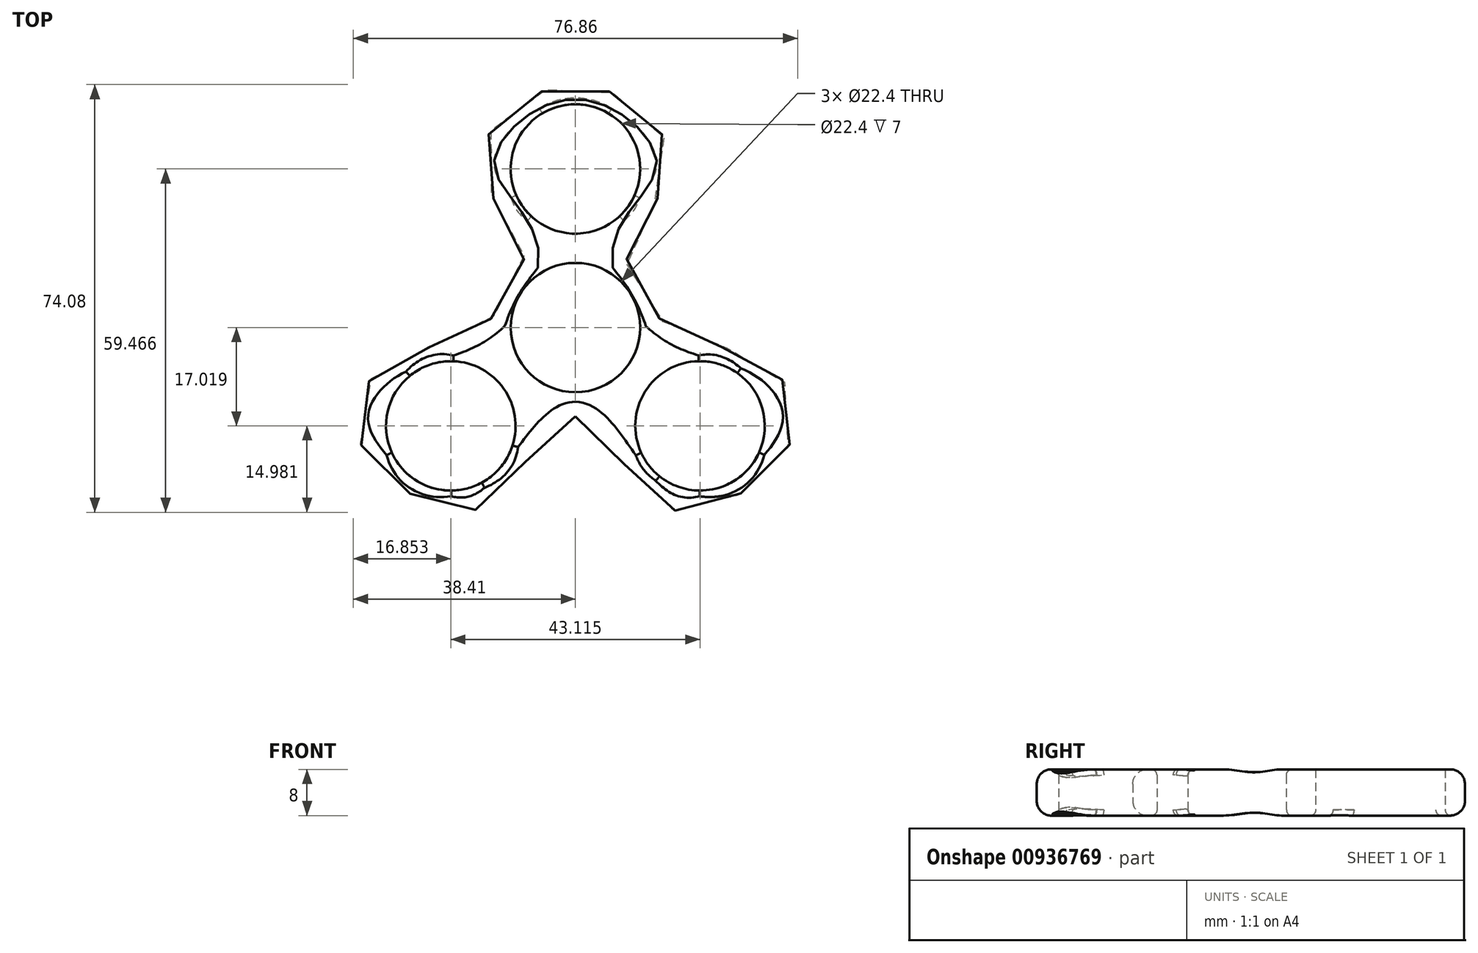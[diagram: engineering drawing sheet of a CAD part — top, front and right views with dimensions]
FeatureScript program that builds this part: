
annotation { "Feature Type Name" : "Feature", "Feature Type Description" : "" }
export const myFeature = defineFeature(function(context is Context, id is Id, definition is map)
    precondition{}
    {
        {
            var Q0;
            Q0=qCreatedBy(makeId("Top.planeOp"),FACE);
            var sketch = newSketch(context, id + "F0", { "sketchPlane" : qUnion([Q0])});
            skCircle(sketch, "E0", {"center": v(0, 0) * mm, "radius": 11.2 * mm});
            skPoint(sketch, "E1", {"position": v(-21.56, -17.02) * mm});
            skPoint(sketch, "E2.MirrorP", {"position": v(21.56, -17.02) * mm});
            skPoint(sketch, "E3", {"position": v(0, 27.47) * mm});
            skCircle(sketch, "E4", {"center": v(0, 27.47) * mm, "radius": 11.2 * mm});
            skCircle(sketch, "E5", {"center": v(21.56, -17.02) * mm, "radius": 11.2 * mm});
            skCircle(sketch, "E6", {"center": v(-21.56, -17.02) * mm, "radius": 11.2 * mm});
            skPoint(sketch, "E7", {"position": v(-16.63, 0) * mm});
            skPoint(sketch, "E8", {"position": v(-16.63, 28.38) * mm});
            skPoint(sketch, "E9", {"position": v(-38.24, -17.32) * mm});
            skPoint(sketch, "E10", {"position": v(-21.9, -31.73) * mm});
            skPoint(sketch, "E11", {"position": v(0, 42.08) * mm});
            skPoint(sketch, "E12", {"position": v(-9.07, 13.96) * mm});
            skPoint(sketch, "E13.MirrorP", {"position": v(16.63, 28.38) * mm});
            skPoint(sketch, "E14.MirrorP", {"position": v(9.07, 13.96) * mm});
            skPoint(sketch, "E15.MirrorP", {"position": v(16.63, 0) * mm});
            skPoint(sketch, "E16.MirrorP", {"position": v(38.24, -17.32) * mm});
            skPoint(sketch, "E17.MirrorP", {"position": v(21.9, -31.73) * mm});
            skPoint(sketch, "E18", {"position": v(0, -15.39) * mm});
            skPoint(sketch, "E19", {"position": v(-31.21, -5.72) * mm});
            skPoint(sketch, "E20", {"position": v(-11.35, -26.81) * mm});
            skPoint(sketch, "E21", {"position": v(31.7, -5.72) * mm});
            skPoint(sketch, "E22", {"position": v(10.8, -26.81) * mm});
            skFitSpline(sketch, "E23", {"points": [v(0, -15.39) * mm, v(-11.35, -26.81) * mm, v(-21.9, -31.73) * mm, v(-38.24, -17.32) * mm, v(-31.21, -5.72) * mm, v(-16.63, 0) * mm, v(-9.07, 13.96) * mm, v(-16.63, 28.38) * mm, v(0, 42.08) * mm, v(16.63, 28.38) * mm, v(9.07, 13.96) * mm, v(16.63, 0) * mm, v(31.7, -5.72) * mm, v(38.24, -17.32) * mm, v(21.9, -31.73) * mm, v(10.8, -26.81) * mm, v(0, -15.39) * mm]});
            skSolve(sketch);
        }
        {
            var Q0;
            Q0=makeQuery(id+"F0.imprint","IMPRINT",FACE,{"disambiguationData":[TD([[makeQuery(id+"F0.imprint","IMPRINT",EDGE,{"derivedFrom":sQuery(id+"F0.wireOp",EDGE,"E0")}),-1.0]])]});
            extrude(context, id + "F1", {"entities" : qUnion([Q0]), "depth" : 8 * mm, "offsetDistance" : 25.4 * mm});
        }
        {
            var Q0;
            Q0=makeQuery(id+"F1.opExtrude","CAP_EDGE",EDGE,{"disambiguationData":[OSD([sQuery(id+"F0.wireOp",EDGE,"E23")])],"isStart":true});
            var Q1;
            Q1=makeQuery(id+"F1.opExtrude","CAP_EDGE",EDGE,{"disambiguationData":[OSD([sQuery(id+"F0.wireOp",EDGE,"E23")])],"isStart":false});
            fillet(context, id + "F2", {"entities" : qUnion([Q0, Q1]), "radius" : 2.54 * mm, "tangentPropagation" : true, "allowEdgeOverflow" : false});
        }
        {
            var Q0;
            Q0=makeQuery(id+"F1.opExtrude","CAP_EDGE",EDGE,{"disambiguationData":[OSD([sQuery(id+"F0.wireOp",EDGE,"E6")])],"isStart":true});
            var Q1;
            Q1=makeQuery(id+"F1.opExtrude","CAP_EDGE",EDGE,{"disambiguationData":[OSD([sQuery(id+"F0.wireOp",EDGE,"E5")])],"isStart":true});
            var Q2;
            Q2=makeQuery(id+"F1.opExtrude","CAP_EDGE",EDGE,{"disambiguationData":[OSD([sQuery(id+"F0.wireOp",EDGE,"E0")])],"isStart":true});
            var Q3;
            Q3=makeQuery(id+"F2.opFillet","BLEND_EDGE",EDGE,{"disambiguationData":[OD(1.0)],"blendedFrom":[makeQuery(id+"F1.opExtrude","CAP_EDGE",EDGE,{"disambiguationData":[OSD([sQuery(id+"F0.wireOp",EDGE,"E23")])],"isStart":true}),makeQuery(id+"F1.opExtrude","SWEPT_FACE",FACE,{"disambiguationData":[OSD([sQuery(id+"F0.wireOp",EDGE,"E0")])]})],"blendedInto":[makeQuery(id+"F1.opExtrude","SWEPT_FACE",FACE,{"disambiguationData":[OSD([sQuery(id+"F0.wireOp",EDGE,"E0")])]})]});
            var Q4;
            Q4=makeQuery(id+"F2.opFillet","BLEND_EDGE",EDGE,{"disambiguationData":[OD(0.0)],"blendedFrom":[makeQuery(id+"F1.opExtrude","CAP_EDGE",EDGE,{"disambiguationData":[OSD([sQuery(id+"F0.wireOp",EDGE,"E23")])],"isStart":true}),makeQuery(id+"F1.opExtrude","SWEPT_FACE",FACE,{"disambiguationData":[OSD([sQuery(id+"F0.wireOp",EDGE,"E0")])]})],"blendedInto":[makeQuery(id+"F1.opExtrude","SWEPT_FACE",FACE,{"disambiguationData":[OSD([sQuery(id+"F0.wireOp",EDGE,"E0")])]})]});
            var Q5;
            Q5=makeQuery(id+"F1.opExtrude","CAP_EDGE",EDGE,{"disambiguationData":[OSD([sQuery(id+"F0.wireOp",EDGE,"E4")])],"isStart":true});
            var Q6;
            Q6=makeQuery(id+"F1.opExtrude","CAP_EDGE",EDGE,{"disambiguationData":[OSD([sQuery(id+"F0.wireOp",EDGE,"E6")])],"isStart":false});
            var Q7;
            Q7=makeQuery(id+"F2.opFillet","BLEND_EDGE",EDGE,{"disambiguationData":[OD(0.0)],"blendedFrom":[makeQuery(id+"F1.opExtrude","CAP_EDGE",EDGE,{"disambiguationData":[OSD([sQuery(id+"F0.wireOp",EDGE,"E23")])],"isStart":false}),makeQuery(id+"F1.opExtrude","SWEPT_FACE",FACE,{"disambiguationData":[OSD([sQuery(id+"F0.wireOp",EDGE,"E0")])]})],"blendedInto":[makeQuery(id+"F1.opExtrude","SWEPT_FACE",FACE,{"disambiguationData":[OSD([sQuery(id+"F0.wireOp",EDGE,"E0")])]})]});
            var Q8;
            Q8=makeQuery(id+"F1.opExtrude","CAP_EDGE",EDGE,{"disambiguationData":[OSD([sQuery(id+"F0.wireOp",EDGE,"E0")])],"isStart":false});
            var Q9;
            Q9=makeQuery(id+"F2.opFillet","BLEND_EDGE",EDGE,{"disambiguationData":[OD(1.0)],"blendedFrom":[makeQuery(id+"F1.opExtrude","CAP_EDGE",EDGE,{"disambiguationData":[OSD([sQuery(id+"F0.wireOp",EDGE,"E23")])],"isStart":false}),makeQuery(id+"F1.opExtrude","SWEPT_FACE",FACE,{"disambiguationData":[OSD([sQuery(id+"F0.wireOp",EDGE,"E0")])]})],"blendedInto":[makeQuery(id+"F1.opExtrude","SWEPT_FACE",FACE,{"disambiguationData":[OSD([sQuery(id+"F0.wireOp",EDGE,"E0")])]})]});
            var Q10;
            Q10=makeQuery(id+"F1.opExtrude","CAP_EDGE",EDGE,{"disambiguationData":[OSD([sQuery(id+"F0.wireOp",EDGE,"E5")])],"isStart":false});
            fillet(context, id + "F3", {"entities" : qUnion([Q0, Q1, Q2, Q3, Q4, Q5, Q6, Q7, Q8, Q9, Q10]), "radius" : 1 * mm, "tangentPropagation" : true, "allowEdgeOverflow" : false});
        }
    });
